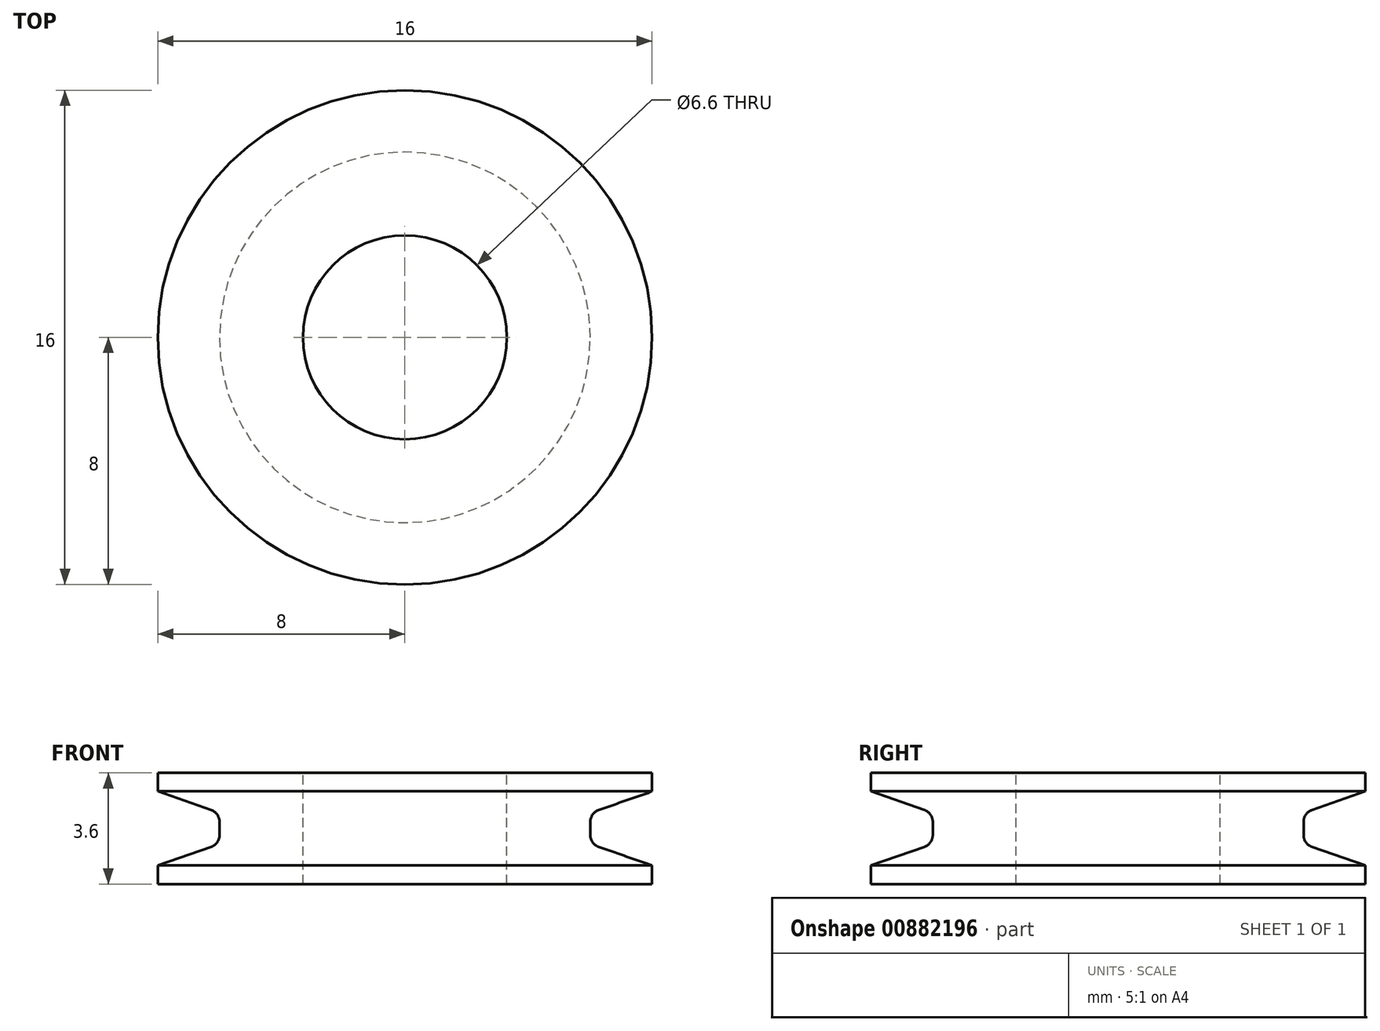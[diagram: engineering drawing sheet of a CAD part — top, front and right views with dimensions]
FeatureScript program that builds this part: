
annotation { "Feature Type Name" : "Feature", "Feature Type Description" : "" }
export const myFeature = defineFeature(function(context is Context, id is Id, definition is map)
    precondition{}
    {
        {
            var Q0;
            Q0=qCreatedBy(makeId("Front.planeOp"),FACE);
            var sketch = newSketch(context, id + "F0", { "sketchPlane" : qUnion([Q0])});
            skLineSegment(sketch, "E0", {"start": v(0, 5.94) * mm, "end": v(0, -5.29) * mm, "construction": true});
            skLineSegment(sketch, "E1", {"start": v(3.3, 0) * mm, "end": v(3.3, 3.6) * mm});
            skLineSegment(sketch, "E2", {"start": v(3.3, 3.6) * mm, "end": v(8, 3.6) * mm});
            skLineSegment(sketch, "E3", {"start": v(8, 3.6) * mm, "end": v(8, 3) * mm});
            skLineSegment(sketch, "E4", {"start": v(8, 3) * mm, "end": v(6.27, 2.4) * mm});
            skLineSegment(sketch, "E5", {"start": v(6, 2.02) * mm, "end": v(6, 1.58) * mm});
            skLineSegment(sketch, "E6", {"start": v(6.27, 1.2) * mm, "end": v(8, 0.6) * mm});
            skLineSegment(sketch, "E7", {"start": v(8, 0.6) * mm, "end": v(8, 0) * mm});
            skLineSegment(sketch, "E8", {"start": v(8, 0) * mm, "end": v(3.3, 0) * mm});
            skPoint(sketch, "E9.visualSharp", {"position": v(6, 2.3) * mm});
            skArc(sketch, "E9.filletArc", {"start": v(6.27, 2.4) * mm, "mid": v(6.07, 2.25) * mm, "end": v(6, 2.02) * mm});
            skPoint(sketch, "E10.visualSharp", {"position": v(6, 1.3) * mm});
            skArc(sketch, "E10.filletArc", {"start": v(6, 1.58) * mm, "mid": v(6.07, 1.35) * mm, "end": v(6.27, 1.2) * mm});
            skSolve(sketch);
        }
        {
            var Q0;
            Q0=qSketchRegion(id+"F0",true);
            var Q1;
            Q1=sQuery(id+"F0.wireOp",EDGE,"E0");
            revolve(context, id + "F1", {"surfaceOperationType" : NewSurfaceOperationType.NEW, "entities" : qUnion([Q0]), "axis" : qUnion([Q1]), "revolveType" : RevolveType.FULL});
        }
    });
